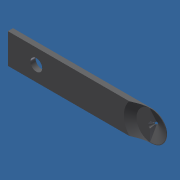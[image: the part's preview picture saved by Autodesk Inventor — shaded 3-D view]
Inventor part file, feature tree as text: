
AUTODESK INVENTOR PART (.ipt)
format: ipt  version: 2015 SP1 (Build 190203100, 203)  size: 397,824 bytes
history: native  units: in
note: dims shown in document units (in); Inventor stores cm internally (conversion verified against a paired STEP export)
features: sketch x6, extrude x4, revolve x3, projected_geometry x3, plane x2, fillet x2, other x2, mirror x1, direct_edit x1, hole x1
ambient origin geometry x8: Origin, YZ Plane, XZ Plane, XY Plane, X Axis, Y Axis, Z Axis, Center Point
bodies: Solid1 (feature_tree)
feature tree (25):
  sketch  "Sketch1"  dims[d0=0.004in d3=0.0945in]
  revolve  "Revolution1"  [1 undecoded]
  plane  "Work Plane4"
  plane  "Work Plane5"
  extrude  "Extrusion1"  TaperAngle=15.0deg  [1 undecoded]
  extrude  "Extrusion2"  Depth=0.454in TaperAngle=0.0deg
  extrude  "Extrusion3"  Depth=1.0in TaperAngle=0.0deg
  revolve  "Revolution2"  Angle=30.0deg
  revolve  "Revolution4"  [1 undecoded]
  mirror  "Mirror2"
  extrude  "Extrusion7"  Depth=0.001in
  fillet  "Fillet4"  Radius=0.008in
  fillet  "Fillet5"  Radius=0.008in
  direct_edit  "Direct Edit1"
  hole  "Hole1"  [1 undecoded]
  sketch  "Sketch2"  dims[d4=0.004in d6=15.0deg]
  projected_geometry  "Projected Loop1"
  projected_geometry  "Projected Loop2"
  sketch  "Sketch4"  dims[d7=180.0deg d8=0.454in d9=0.0in]
  sketch  "Sketch7"  dims[d10=1.0in d11=0.0in d12=1.0in d13=0.0in]
  sketch  "Sketch9"  dims[d14=0.1374in d15=30.0deg]
  projected_geometry  "Projected Loop3"
  sketch  "Sketch10"  dims[d16=90.0deg d19=0.2376in d22=0.004in d34=0.008in d35=0.008in d39=0.008in d40=0.008in d42=0.082in d43=2.2in d45=30.0deg d47=0.008in d48=180.0deg d53=0.078in d54=0.0in d56=0.001in d57=0.004in d58=1.75in d59=0.1875in d60=0.75in d61=0.375in d62=0.25in d63=0.5635in d64=1.0in d65=0.8108in d67=0.035in]
  other  "Delete1"
  other  "Delete2"
note: 4 required parameter values undecoded (feature->parameter linkage not recoverable at this tier; creation-order binding heuristic only, values carry confidence <= 0.55)